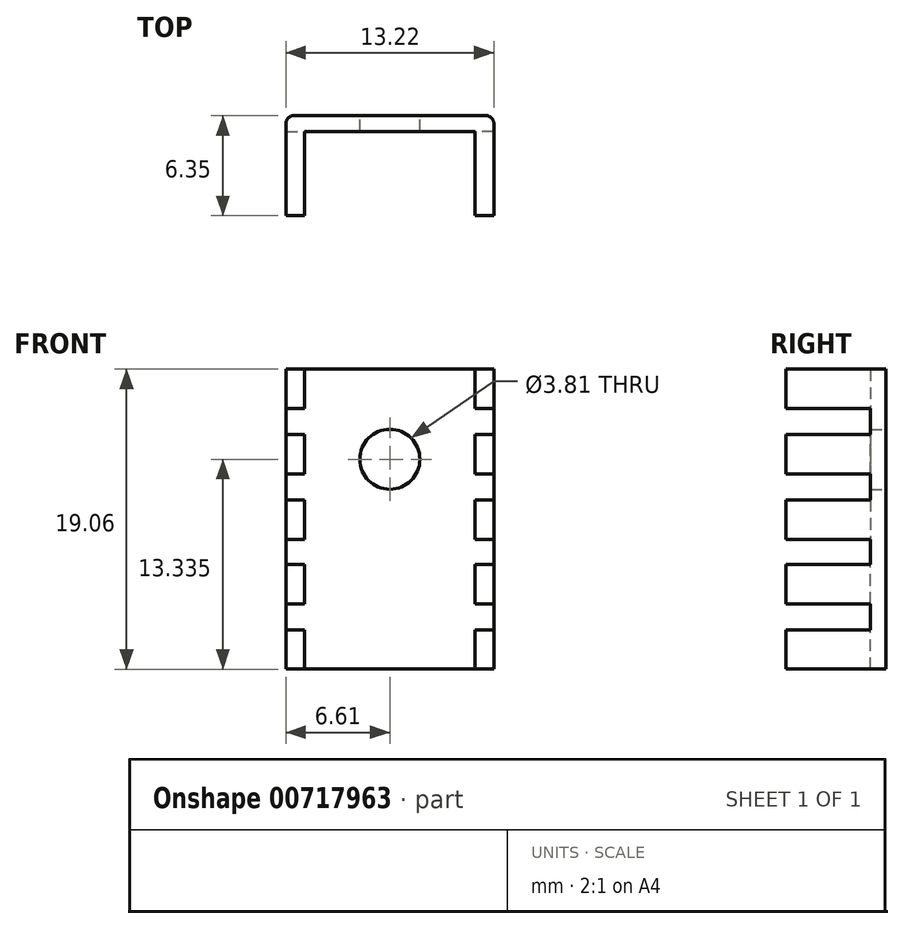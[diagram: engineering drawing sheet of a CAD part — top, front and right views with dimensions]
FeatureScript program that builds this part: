
annotation { "Feature Type Name" : "Feature", "Feature Type Description" : "" }
export const myFeature = defineFeature(function(context is Context, id is Id, definition is map)
    precondition{}
    {
        {
            var Q0;
            Q0=qCreatedBy(makeId("Front.planeOp"),FACE);
            var sketch = newSketch(context, id + "F0", { "sketchPlane" : qUnion([Q0])});
            skLineSegment(sketch, "E0.bottom", {"start": v(6.6, -9.53) * mm, "end": v(-6.6, -9.53) * mm});
            skLineSegment(sketch, "E0.top", {"start": v(6.6, 9.53) * mm, "end": v(-6.6, 9.53) * mm});
            skLineSegment(sketch, "E0.left", {"start": v(6.6, -9.52) * mm, "end": v(6.6, 9.53) * mm});
            skLineSegment(sketch, "E0.right", {"start": v(-6.6, -9.53) * mm, "end": v(-6.6, 9.53) * mm});
            skPoint(sketch, "E0.middle", {"position": v(0, 0) * mm});
            skSolve(sketch);
        }
        {
            var Q0;
            Q0 = qSketchRegion(id + "F0", true);
            extrude(context, id + "F1", {"entities" : qUnion([Q0]), "depth" : 1 * mm, "offsetDistance" : 25 * mm});
        }
        {
            var Q0;
            Q0=makeQuery(id+"F1.opExtrude","CAP_FACE",FACE,{"disambiguationData":[OSD([sQuery(id+"F0.wireOp",EDGE,"E0.bottom"),sQuery(id+"F0.wireOp",EDGE,"E0.top"),sQuery(id+"F0.wireOp",EDGE,"E0.left"),sQuery(id+"F0.wireOp",EDGE,"E0.right")])],"isStart":false});
            var sketch = newSketch(context, id + "F2", { "sketchPlane" : qUnion([Q0])});
            skLineSegment(sketch, "E1.bottom", {"start": v(6.6, 9.53) * mm, "end": v(5.4, 9.53) * mm});
            skLineSegment(sketch, "E1.top", {"start": v(6.6, 7.03) * mm, "end": v(5.4, 7.03) * mm});
            skLineSegment(sketch, "E1.left", {"start": v(6.6, 9.53) * mm, "end": v(6.6, 7.03) * mm});
            skLineSegment(sketch, "E1.right", {"start": v(5.4, 9.53) * mm, "end": v(5.4, 7.03) * mm});
            skLineSegment(sketch, "E2.bottom", {"start": v(6.6, 5.38) * mm, "end": v(5.4, 5.38) * mm});
            skLineSegment(sketch, "E2.top", {"start": v(6.6, 2.88) * mm, "end": v(5.4, 2.88) * mm});
            skLineSegment(sketch, "E2.left", {"start": v(6.6, 5.38) * mm, "end": v(6.6, 2.88) * mm});
            skLineSegment(sketch, "E2.right", {"start": v(5.4, 5.38) * mm, "end": v(5.4, 2.88) * mm});
            skLineSegment(sketch, "E3.bottom", {"start": v(6.6, 1.23) * mm, "end": v(5.4, 1.23) * mm});
            skLineSegment(sketch, "E3.top", {"start": v(6.6, -1.27) * mm, "end": v(5.4, -1.27) * mm});
            skLineSegment(sketch, "E3.left", {"start": v(6.6, 1.23) * mm, "end": v(6.6, -1.27) * mm});
            skLineSegment(sketch, "E3.right", {"start": v(5.4, 1.23) * mm, "end": v(5.4, -1.27) * mm});
            skLineSegment(sketch, "E4", {"start": v(0, 11.51) * mm, "end": v(0, -11.5) * mm, "construction": true});
            skLineSegment(sketch, "E5", {"start": v(12.38, 0) * mm, "end": v(-11.57, 0) * mm, "construction": true});
            skLineSegment(sketch, "E6.MirrorCS", {"start": v(5.4, -1.23) * mm, "end": v(5.4, 1.27) * mm});
            skLineSegment(sketch, "E7.MirrorCS", {"start": v(6.6, -2.88) * mm, "end": v(5.4, -2.88) * mm});
            skLineSegment(sketch, "E8.MirrorCS", {"start": v(5.4, -5.38) * mm, "end": v(5.4, -2.88) * mm});
            skLineSegment(sketch, "E9.MirrorCS", {"start": v(6.6, -5.38) * mm, "end": v(6.6, -2.88) * mm});
            skLineSegment(sketch, "E10.MirrorCS", {"start": v(6.6, -5.38) * mm, "end": v(5.4, -5.38) * mm});
            skLineSegment(sketch, "E11.MirrorCS", {"start": v(6.6, -7.03) * mm, "end": v(5.4, -7.03) * mm});
            skLineSegment(sketch, "E12.MirrorCS", {"start": v(5.4, -9.53) * mm, "end": v(5.4, -7.03) * mm});
            skLineSegment(sketch, "E13.MirrorCS", {"start": v(6.6, -9.53) * mm, "end": v(6.6, -7.03) * mm});
            skLineSegment(sketch, "E14.MirrorCS", {"start": v(6.6, -9.53) * mm, "end": v(5.4, -9.53) * mm});
            skLineSegment(sketch, "E15.MirrorCS", {"start": v(-5.4, 9.53) * mm, "end": v(-5.4, 7.03) * mm});
            skLineSegment(sketch, "E16.MirrorCS", {"start": v(-6.6, 7.03) * mm, "end": v(-5.4, 7.03) * mm});
            skLineSegment(sketch, "E17.MirrorCS", {"start": v(-6.6, 9.53) * mm, "end": v(-6.6, 7.03) * mm});
            skLineSegment(sketch, "E18.MirrorCS", {"start": v(-6.6, 9.53) * mm, "end": v(-5.4, 9.53) * mm});
            skLineSegment(sketch, "E19.MirrorCS", {"start": v(-6.6, 5.38) * mm, "end": v(-5.4, 5.38) * mm});
            skLineSegment(sketch, "E20.MirrorCS", {"start": v(-5.4, 5.38) * mm, "end": v(-5.4, 2.88) * mm});
            skLineSegment(sketch, "E21.MirrorCS", {"start": v(-6.6, 5.38) * mm, "end": v(-6.6, 2.88) * mm});
            skLineSegment(sketch, "E22.MirrorCS", {"start": v(-6.6, 2.88) * mm, "end": v(-5.4, 2.88) * mm});
            skLineSegment(sketch, "E23.MirrorCS", {"start": v(-6.6, 1.23) * mm, "end": v(-5.4, 1.23) * mm});
            skLineSegment(sketch, "E24.MirrorCS", {"start": v(-5.4, 1.23) * mm, "end": v(-5.4, -1.27) * mm});
            skLineSegment(sketch, "E25.MirrorCS", {"start": v(-6.6, -1.27) * mm, "end": v(-5.4, -1.27) * mm});
            skLineSegment(sketch, "E26.MirrorCS", {"start": v(-6.6, 1.23) * mm, "end": v(-6.6, -1.27) * mm});
            skLineSegment(sketch, "E27.MirrorCS", {"start": v(-6.6, -2.88) * mm, "end": v(-5.4, -2.88) * mm});
            skLineSegment(sketch, "E28.MirrorCS", {"start": v(-5.4, -5.38) * mm, "end": v(-5.4, -2.88) * mm});
            skLineSegment(sketch, "E29.MirrorCS", {"start": v(-6.6, -5.38) * mm, "end": v(-6.6, -2.88) * mm});
            skLineSegment(sketch, "E30.MirrorCS", {"start": v(-6.6, -5.38) * mm, "end": v(-5.4, -5.38) * mm});
            skLineSegment(sketch, "E31.MirrorCS", {"start": v(-6.6, -9.53) * mm, "end": v(-6.6, -7.03) * mm});
            skLineSegment(sketch, "E32.MirrorCS", {"start": v(-5.4, -9.53) * mm, "end": v(-5.4, -7.03) * mm});
            skLineSegment(sketch, "E33.MirrorCS", {"start": v(-6.6, -7.03) * mm, "end": v(-5.4, -7.03) * mm});
            skLineSegment(sketch, "E34.MirrorCS", {"start": v(-6.6, -9.53) * mm, "end": v(-5.4, -9.53) * mm});
            skSolve(sketch);
        }
        {
            var Q0;
            Q0 = qSketchRegion(id + "F2", true);
            extrude(context, id + "F3", {"entities" : qUnion([Q0]), "operationType" : NewBodyOperationType.ADD, "depth" : 5.35 * mm, "offsetDistance" : 25 * mm});
        }
        {
            var Q0;
            Q0=makeQuery(id+"F1.opExtrude","CAP_EDGE",EDGE,{"disambiguationData":[OSD([sQuery(id+"F0.wireOp",EDGE,"E0.left")])],"isStart":true});
            var Q1;
            Q1=makeQuery(id+"F1.opExtrude","CAP_EDGE",EDGE,{"disambiguationData":[OSD([sQuery(id+"F0.wireOp",EDGE,"E0.right")])],"isStart":true});
            fillet(context, id + "F4", {"entities" : qUnion([Q0, Q1]), "radius" : 0.5 * mm, "tangentPropagation" : true, "allowEdgeOverflow" : false});
        }
        {
            var Q0;
            Q0=makeQuery(id+"F1.opExtrude","CAP_FACE",FACE,{"disambiguationData":[OSD([sQuery(id+"F0.wireOp",EDGE,"E0.bottom"),sQuery(id+"F0.wireOp",EDGE,"E0.top"),sQuery(id+"F0.wireOp",EDGE,"E0.left"),sQuery(id+"F0.wireOp",EDGE,"E0.right")])],"isStart":true});
            var sketch = newSketch(context, id + "F5", { "sketchPlane" : qUnion([Q0])});
            skPoint(sketch, "E35", {"position": v(0, 3.8) * mm});
            skSolve(sketch);
        }
        {
            var Q0;
            Q0=sQuery(id+"F5.wireOp",VERTEX,"E35");
            var Q1;
            Q1=makeQuery(id+"F1.opExtrude","SWEPT_BODY",BODY,{"disambiguationData":[OSD([sQuery(id+"F0.wireOp",EDGE,"E0.bottom"),sQuery(id+"F0.wireOp",EDGE,"E0.top"),sQuery(id+"F0.wireOp",EDGE,"E0.left"),sQuery(id+"F0.wireOp",EDGE,"E0.right")])]});
            hole(context, id + "F6", {"style" : HoleStyle.SIMPLE, "endStyle" : HoleEndStyle.THROUGH, "holeDiameter" : 3.81 * mm, "majorDiameter" : 5 * mm, "isTappedThrough" : true, "tappedDepth" : 12 * mm, "tapClearance" : 3, "locations" : qUnion([Q0]), "scope" : qUnion([Q1])});
        }
    });
